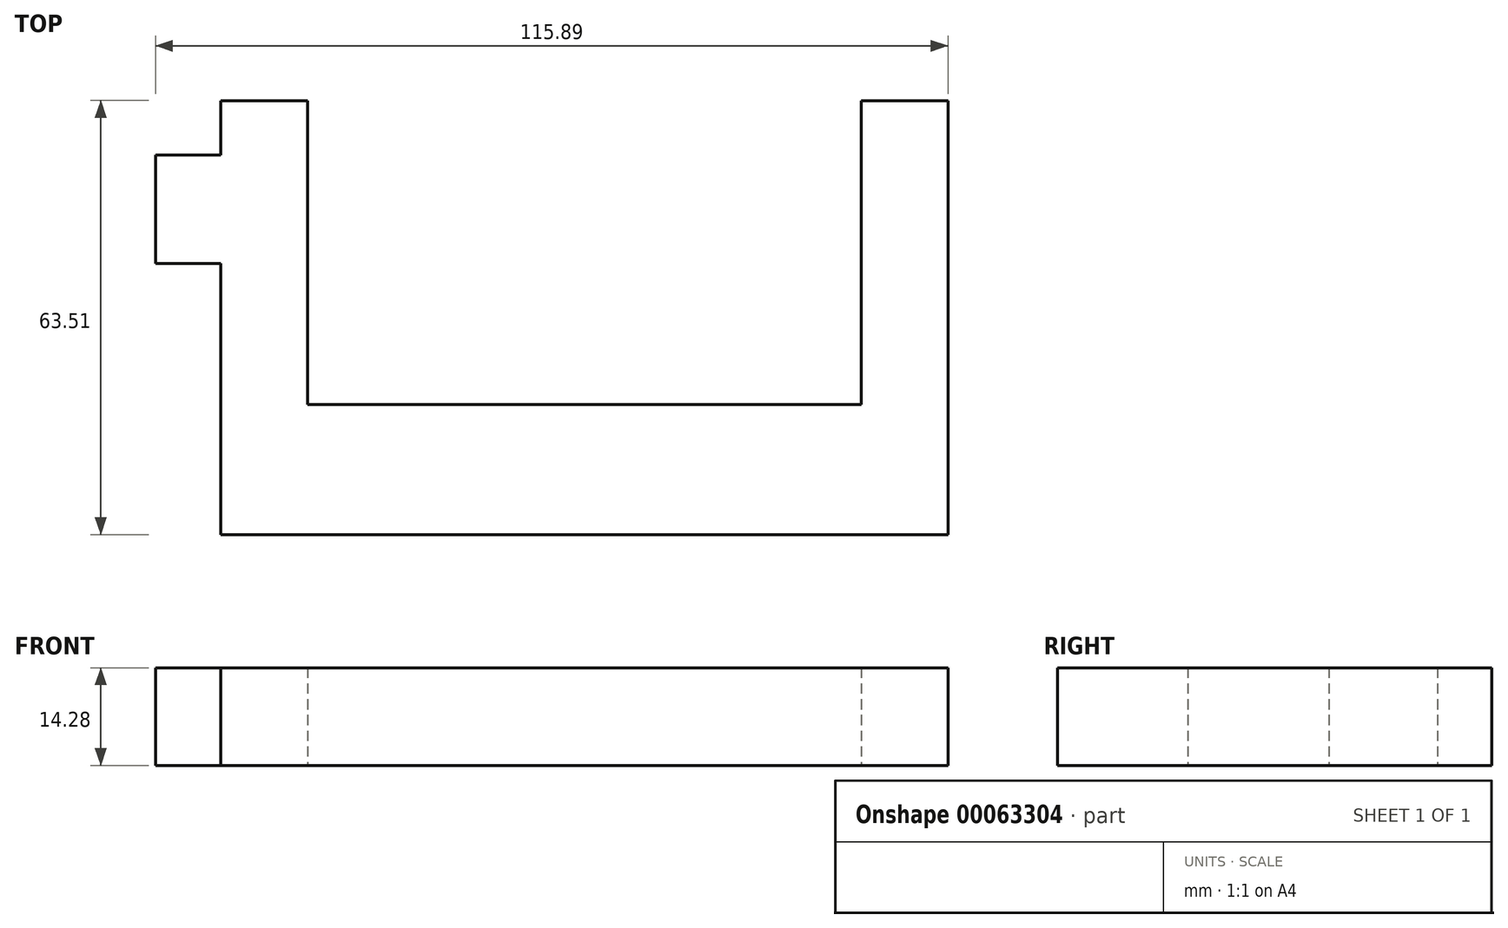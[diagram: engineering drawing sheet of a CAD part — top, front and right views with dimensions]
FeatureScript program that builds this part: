
annotation { "Feature Type Name" : "Feature", "Feature Type Description" : "" }
export const myFeature = defineFeature(function(context is Context, id is Id, definition is map)
    precondition{}
    {
        {
            var Q0;
            Q0=qCreatedBy(makeId("Top.planeOp"),FACE);
            var sketch = newSketch(context, id + "F0", { "sketchPlane" : qUnion([Q0])});
            skLineSegment(sketch, "E0.rect.bottom", {"start": v(40.48, 9.52) * mm, "end": v(-40.48, 9.52) * mm});
            skLineSegment(sketch, "E0.rect.top", {"start": v(53.18, -9.53) * mm, "end": v(-53.18, -9.53) * mm});
            skLineSegment(sketch, "E0.rect.left", {"start": v(53.18, 9.52) * mm, "end": v(53.18, -9.53) * mm});
            skLineSegment(sketch, "E0.rect.right", {"start": v(-53.18, 9.52) * mm, "end": v(-53.18, -9.53) * mm});
            skPoint(sketch, "E0.rect.middle", {"position": v(0, 0) * mm});
            skLineSegment(sketch, "E1.bottom", {"start": v(53.18, -9.53) * mm, "end": v(40.48, -9.53) * mm});
            skLineSegment(sketch, "E1.top", {"start": v(53.18, 53.98) * mm, "end": v(40.48, 53.98) * mm});
            skLineSegment(sketch, "E1.left", {"start": v(53.18, -9.53) * mm, "end": v(53.18, 53.98) * mm});
            skLineSegment(sketch, "E1.right", {"start": v(40.48, 9.52) * mm, "end": v(40.48, 53.97) * mm});
            skLineSegment(sketch, "E2.bottom", {"start": v(-53.18, -9.53) * mm, "end": v(-40.48, -9.53) * mm});
            skLineSegment(sketch, "E2.top", {"start": v(-53.18, 53.97) * mm, "end": v(-40.48, 53.97) * mm});
            skLineSegment(sketch, "E2.left", {"start": v(-53.18, -9.53) * mm, "end": v(-53.18, 53.97) * mm});
            skLineSegment(sketch, "E2.right", {"start": v(-40.48, 9.52) * mm, "end": v(-40.48, 53.97) * mm});
            skSolve(sketch);
        }
        {
            var Q0;
            Q0=makeQuery(id+"F0.imprint","IMPRINT",FACE,{"disambiguationData":[TD([[makeQuery(id+"F0.imprint","IMPRINT",EDGE,{"derivedFrom":sQuery(id+"F0.wireOp",EDGE,"E0.rect.bottom")}),1.0]])]});
            extrude(context, id + "F1", {"entities" : qUnion([Q0]), "depth" : 14.29 * mm, "symmetric" : true});
        }
        {
            var Q0;
            Q0=makeQuery(id+"F1.opExtrude","SWEPT_FACE",FACE,{"disambiguationData":[OSD([sQuery(id+"F0.wireOp",EDGE,"E2.left")])]});
            var sketch = newSketch(context, id + "F2", { "sketchPlane" : qUnion([Q0])});
            skLineSegment(sketch, "E3.rect.bottom", {"start": v(-30.16, 7.14) * mm, "end": v(-46.04, 7.14) * mm});
            skLineSegment(sketch, "E3.rect.top", {"start": v(-30.16, -7.14) * mm, "end": v(-46.04, -7.14) * mm});
            skLineSegment(sketch, "E3.rect.left", {"start": v(-30.16, 7.14) * mm, "end": v(-30.16, -7.14) * mm});
            skLineSegment(sketch, "E3.rect.right", {"start": v(-46.04, 7.14) * mm, "end": v(-46.04, -7.14) * mm});
            skPoint(sketch, "E3.rect.middle", {"position": v(-38.1, 0) * mm});
            skSolve(sketch);
        }
        {
            var Q0;
            Q0 = qSketchRegion(id + "F2", true);
            extrude(context, id + "F3", {"entities" : qUnion([Q0]), "operationType" : NewBodyOperationType.ADD, "depth" : 9.52 * mm});
        }
    });
